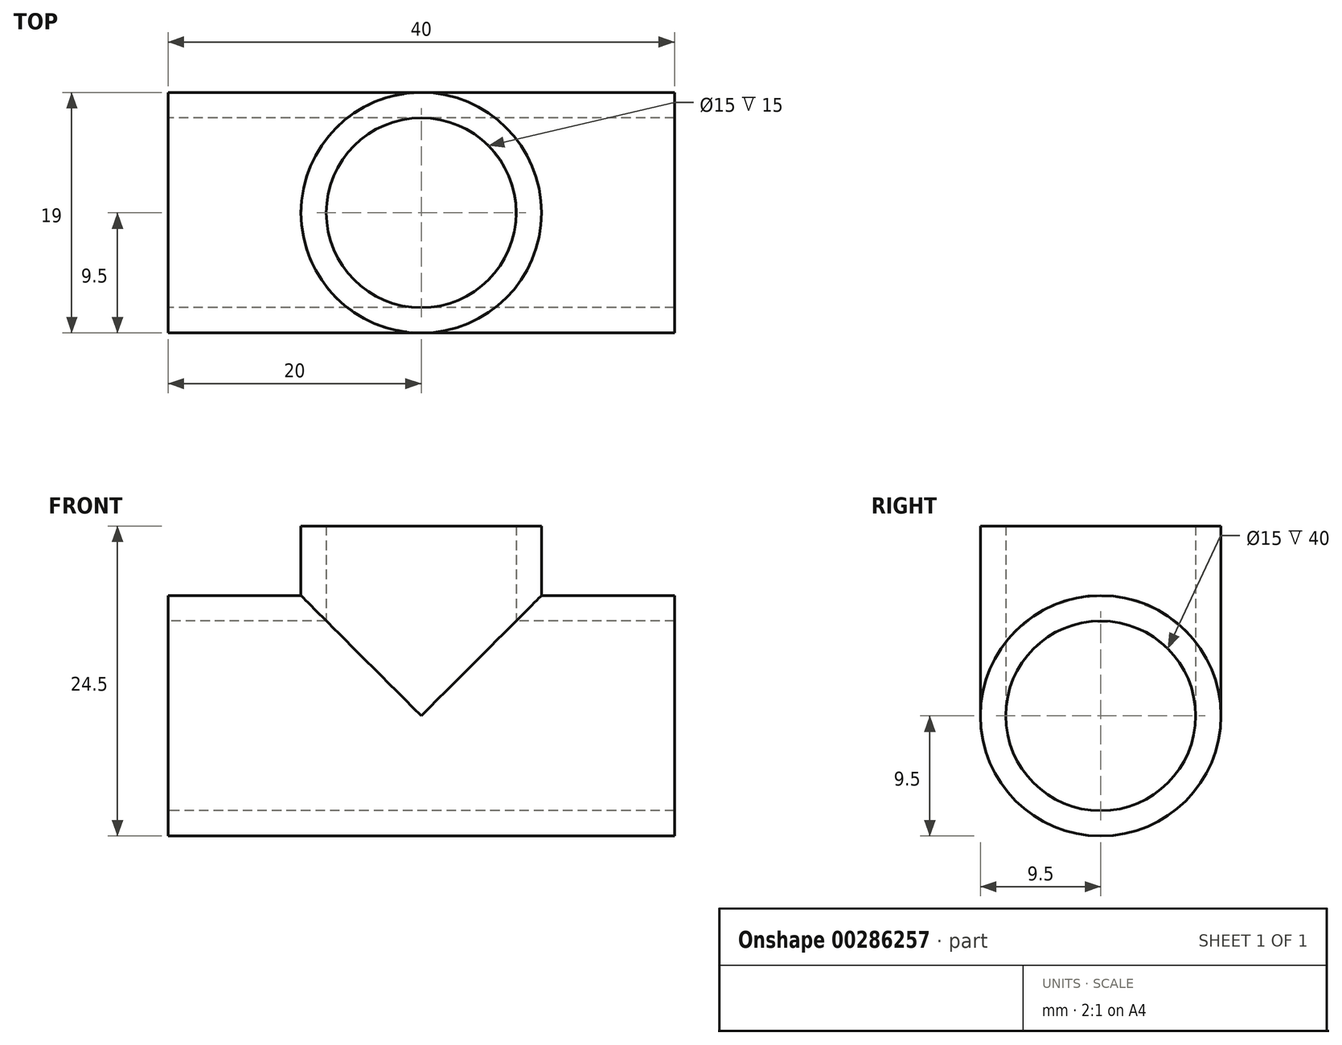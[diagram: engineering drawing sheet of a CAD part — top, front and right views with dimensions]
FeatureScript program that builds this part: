
annotation { "Feature Type Name" : "Feature", "Feature Type Description" : "" }
export const myFeature = defineFeature(function(context is Context, id is Id, definition is map)
    precondition{}
    {
        {
            var Q0;
            Q0=qCreatedBy(makeId("Right.planeOp"),FACE);
            var sketch = newSketch(context, id + "F0", { "sketchPlane" : qUnion([Q0])});
            skCircle(sketch, "E0", {"center": v(0, 0) * mm, "radius": 7.5 * mm});
            skCircle(sketch, "E1", {"center": v(0, 0) * mm, "radius": 9.5 * mm});
            skSolve(sketch);
        }
        {
            var Q0;
            Q0 = qSketchRegion(id + "F0", true);
            extrude(context, id + "F1", {"entities" : qUnion([Q0]), "depth" : 40 * mm});
        }
        {
            var Q0;
            Q0=qCreatedBy(makeId("Top.planeOp"),FACE);
            var sketch = newSketch(context, id + "F2", { "sketchPlane" : qUnion([Q0])});
            skCircle(sketch, "E2", {"center": v(20, 0) * mm, "radius": 7.5 * mm});
            skCircle(sketch, "E3", {"center": v(20, 0) * mm, "radius": 9.5 * mm});
            skLineSegment(sketch, "E4", {"start": v(0, 0) * mm, "end": v(20, 0) * mm, "construction": true});
            skLineSegment(sketch, "E5", {"start": v(40, 0) * mm, "end": v(20, 0) * mm, "construction": true});
            skSolve(sketch);
        }
        {
            var Q0;
            Q0 = qSketchRegion(id + "F2", true);
            extrude(context, id + "F3", {"entities" : qUnion([Q0]), "operationType" : NewBodyOperationType.ADD, "depth" : 15 * mm});
        }
        {
            var Q0;
            Q0=makeQuery(id+"F1.opExtrude","CAP_FACE",FACE,{"disambiguationData":[OSD([sQuery(id+"F0.wireOp",EDGE,"E0"),sQuery(id+"F0.wireOp",EDGE,"E1")])],"isStart":false});
            var sketch = newSketch(context, id + "F4", { "sketchPlane" : qUnion([Q0])});
            skCircle(sketch, "E6", {"center": v(0, 0) * mm, "radius": 7.5 * mm});
            skSolve(sketch);
        }
        {
            var Q0;
            Q0 = qSketchRegion(id + "F4", true);
            extrude(context, id + "F5", {"entities" : qUnion([Q0]), "operationType" : NewBodyOperationType.REMOVE, "oppositeDirection" : true, "depth" : 50 * mm});
        }
        {
            var Q0;
            Q0=makeQuery(id+"F3.opExtrude","CAP_FACE",FACE,{"disambiguationData":[OSD([sQuery(id+"F2.wireOp",EDGE,"E2"),sQuery(id+"F2.wireOp",EDGE,"E3")])],"isStart":false});
            var sketch = newSketch(context, id + "F6", { "sketchPlane" : qUnion([Q0])});
            skCircle(sketch, "E7", {"center": v(20, 0) * mm, "radius": 7.5 * mm});
            skSolve(sketch);
        }
        {
            var Q0;
            Q0 = qSketchRegion(id + "F6", true);
            extrude(context, id + "F7", {"entities" : qUnion([Q0]), "operationType" : NewBodyOperationType.REMOVE, "oppositeDirection" : true, "depth" : 15 * mm});
        }
    });
